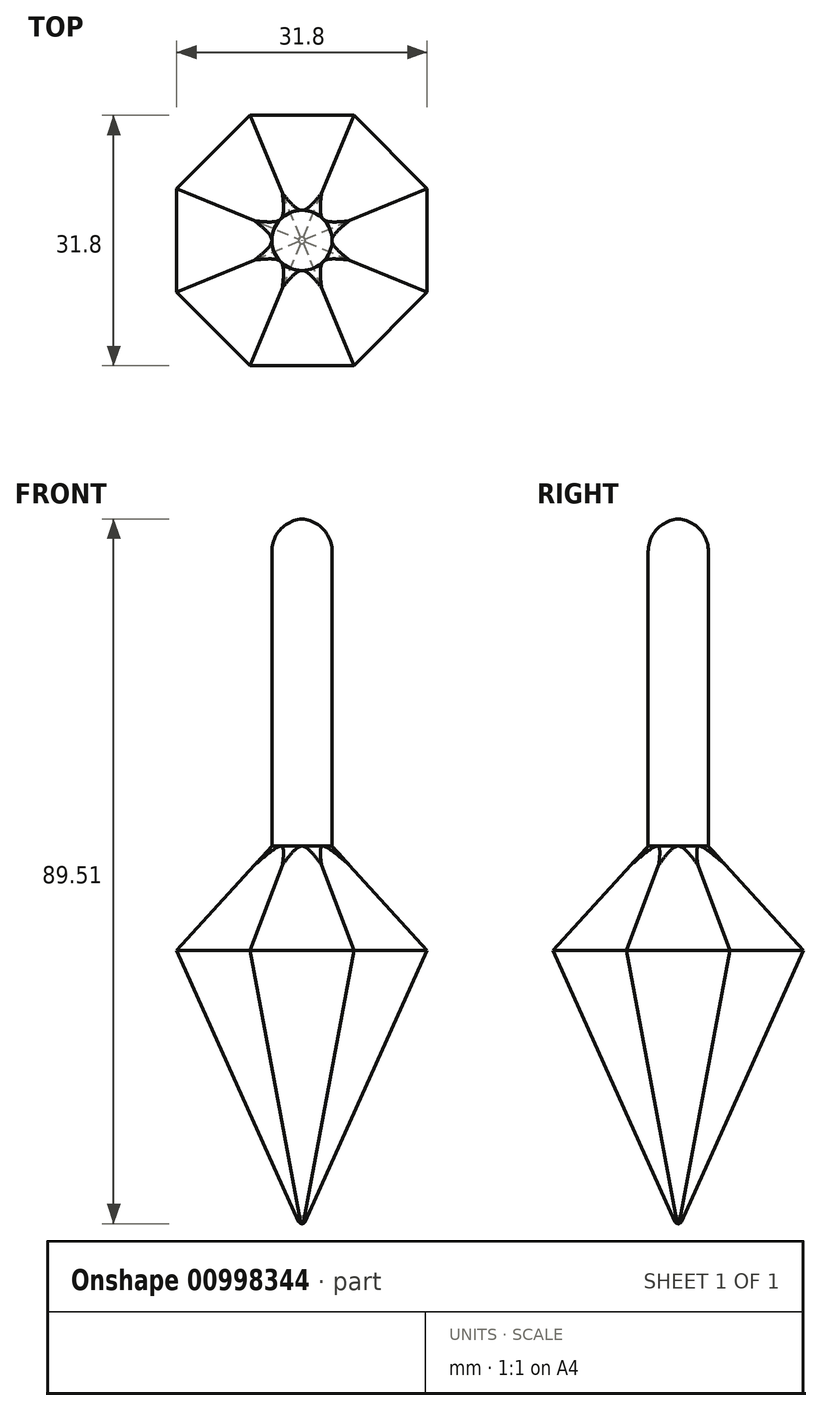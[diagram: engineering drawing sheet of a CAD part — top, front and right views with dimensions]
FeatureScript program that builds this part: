
annotation { "Feature Type Name" : "Feature", "Feature Type Description" : "" }
export const myFeature = defineFeature(function(context is Context, id is Id, definition is map)
    precondition{}
    {
        {
            var Q0;
            Q0=qCreatedBy(makeId("Front.planeOp"),FACE);
            var sketch = newSketch(context, id + "F0", { "sketchPlane" : qUnion([Q0])});
            skLineSegment(sketch, "E0", {"start": v(0, 0) * mm, "end": v(-18.62, 35.4) * mm});
            skLineSegment(sketch, "E1", {"start": v(-18.62, 35.4) * mm, "end": v(-3.83, 48.61) * mm});
            skLineSegment(sketch, "E2", {"start": v(-3.83, 48.61) * mm, "end": v(-3.83, 86.06) * mm});
            skLineSegment(sketch, "E3", {"start": v(0, 86.06) * mm, "end": v(0, 0) * mm});
            skArc(sketch, "E4", {"start": v(0, 90.17) * mm, "mid": v(-2.72, 88.86) * mm, "end": v(-3.83, 86.06) * mm});
            skLineSegment(sketch, "E5", {"start": v(0, 90.17) * mm, "end": v(0, 86.06) * mm});
            skLineSegment(sketch, "E6", {"start": v(0, 0) * mm, "end": v(-41.43, 0) * mm, "construction": true});
            skSolve(sketch);
        }
        {
            var Q0;
            Q0=makeQuery(id+"F0.imprint","IMPRINT",FACE,{"disambiguationData":[TD([[makeQuery(id+"F0.imprint","IMPRINT",EDGE,{"derivedFrom":sQuery(id+"F0.wireOp",EDGE,"E0")}),-1.0]])]});
            var Q1;
            Q1=sQuery(id+"F0.wireOp",EDGE,"E3");
            revolve(context, id + "F1", {"surfaceOperationType" : NewSurfaceOperationType.NEW, "entities" : qUnion([Q0]), "axis" : qUnion([Q1]), "revolveType" : RevolveType.FULL});
        }
        {
            var Q0;
            Q0=qCreatedBy(makeId("Front.planeOp"),FACE);
            var sketch = newSketch(context, id + "F2", { "sketchPlane" : qUnion([Q0])});
            skLineSegment(sketch, "E7", {"start": v(0, 0) * mm, "end": v(-15.9, 35.38) * mm});
            skLineSegment(sketch, "E8", {"start": v(-15.9, 35.38) * mm, "end": v(-23.42, 35.38) * mm});
            skLineSegment(sketch, "E9", {"start": v(-23.42, 35.38) * mm, "end": v(0, 0) * mm});
            skLineSegment(sketch, "E10", {"start": v(-15.9, 35.38) * mm, "end": v(-3.83, 48.61) * mm});
            skLineSegment(sketch, "E11", {"start": v(-3.83, 48.61) * mm, "end": v(-23.42, 35.38) * mm});
            skSolve(sketch);
        }
        {
            var Q0;
            Q0 = qSketchRegion(id + "F2", true);
            extrude(context, id + "F3", {"entities" : qUnion([Q0]), "endBound" : BoundingType.SYMMETRIC, "depth" : 26 * mm, "offsetDistance" : 25 * mm});
        }
        {
            var Q0;
            Q0=makeQuery(id+"F3.opExtrude","SWEPT_BODY",BODY,{"disambiguationData":[OSD([sQuery(id+"F2.wireOp",EDGE,"E7"),sQuery(id+"F2.wireOp",EDGE,"E9"),sQuery(id+"F2.wireOp",EDGE,"E10"),sQuery(id+"F2.wireOp",EDGE,"E11")])]});
            var Q1;
            Q1=makeQuery(id+"F1.opRevolve","SWEPT_EDGE",EDGE,{"disambiguationData":[OSD([sQuery(id+"F0.wireOp",EDGE,"E0"),sQuery(id+"F0.wireOp",EDGE,"E1")])]});
            circularPattern(context, id + "F4", {"entities" : qUnion([Q0]), "axis" : qUnion([Q1]), "angle" : 360 * degree, "instanceCount" : 8, "equalSpace" : true});
        }
        {
            var Q0;
            Q0=makeQuery(id+"F3.opExtrude","SWEPT_BODY",BODY,{"disambiguationData":[OSD([sQuery(id+"F2.wireOp",EDGE,"E7"),sQuery(id+"F2.wireOp",EDGE,"E9"),sQuery(id+"F2.wireOp",EDGE,"E10"),sQuery(id+"F2.wireOp",EDGE,"E11")])]});
            var Q1;
            Q1=makeQuery(id+"F4.opPattern","COPY",BODY,{"derivedFrom":makeQuery(id+"F3.opExtrude","SWEPT_BODY",BODY,{"disambiguationData":[OSD([sQuery(id+"F2.wireOp",EDGE,"E7"),sQuery(id+"F2.wireOp",EDGE,"E9"),sQuery(id+"F2.wireOp",EDGE,"E10"),sQuery(id+"F2.wireOp",EDGE,"E11")])]}),"instanceName":"1"});
            var Q2;
            Q2=makeQuery(id+"F4.opPattern","COPY",BODY,{"derivedFrom":makeQuery(id+"F3.opExtrude","SWEPT_BODY",BODY,{"disambiguationData":[OSD([sQuery(id+"F2.wireOp",EDGE,"E7"),sQuery(id+"F2.wireOp",EDGE,"E9"),sQuery(id+"F2.wireOp",EDGE,"E10"),sQuery(id+"F2.wireOp",EDGE,"E11")])]}),"instanceName":"2"});
            var Q3;
            Q3=makeQuery(id+"F4.opPattern","COPY",BODY,{"derivedFrom":makeQuery(id+"F3.opExtrude","SWEPT_BODY",BODY,{"disambiguationData":[OSD([sQuery(id+"F2.wireOp",EDGE,"E7"),sQuery(id+"F2.wireOp",EDGE,"E9"),sQuery(id+"F2.wireOp",EDGE,"E10"),sQuery(id+"F2.wireOp",EDGE,"E11")])]}),"instanceName":"3"});
            var Q4;
            Q4=makeQuery(id+"F4.opPattern","COPY",BODY,{"derivedFrom":makeQuery(id+"F3.opExtrude","SWEPT_BODY",BODY,{"disambiguationData":[OSD([sQuery(id+"F2.wireOp",EDGE,"E7"),sQuery(id+"F2.wireOp",EDGE,"E9"),sQuery(id+"F2.wireOp",EDGE,"E10"),sQuery(id+"F2.wireOp",EDGE,"E11")])]}),"instanceName":"4"});
            var Q5;
            Q5=makeQuery(id+"F4.opPattern","COPY",BODY,{"derivedFrom":makeQuery(id+"F3.opExtrude","SWEPT_BODY",BODY,{"disambiguationData":[OSD([sQuery(id+"F2.wireOp",EDGE,"E7"),sQuery(id+"F2.wireOp",EDGE,"E9"),sQuery(id+"F2.wireOp",EDGE,"E10"),sQuery(id+"F2.wireOp",EDGE,"E11")])]}),"instanceName":"5"});
            var Q6;
            Q6=makeQuery(id+"F4.opPattern","COPY",BODY,{"derivedFrom":makeQuery(id+"F3.opExtrude","SWEPT_BODY",BODY,{"disambiguationData":[OSD([sQuery(id+"F2.wireOp",EDGE,"E7"),sQuery(id+"F2.wireOp",EDGE,"E9"),sQuery(id+"F2.wireOp",EDGE,"E10"),sQuery(id+"F2.wireOp",EDGE,"E11")])]}),"instanceName":"6"});
            var Q7;
            Q7=makeQuery(id+"F4.opPattern","COPY",BODY,{"derivedFrom":makeQuery(id+"F3.opExtrude","SWEPT_BODY",BODY,{"disambiguationData":[OSD([sQuery(id+"F2.wireOp",EDGE,"E7"),sQuery(id+"F2.wireOp",EDGE,"E9"),sQuery(id+"F2.wireOp",EDGE,"E10"),sQuery(id+"F2.wireOp",EDGE,"E11")])]}),"instanceName":"7"});
            var Q8;
            Q8=makeQuery(id+"F1.opRevolve","SWEPT_BODY",BODY,{"disambiguationData":[OSD([sQuery(id+"F0.wireOp",EDGE,"E0"),sQuery(id+"F0.wireOp",EDGE,"E1"),sQuery(id+"F0.wireOp",EDGE,"E2"),sQuery(id+"F0.wireOp",EDGE,"E3"),sQuery(id+"F0.wireOp",EDGE,"E4"),sQuery(id+"F0.wireOp",EDGE,"E5")])]});
            booleanBodies(context, id + "F5", {"operationType" : BooleanOperationType.SUBTRACTION, "tools" : qUnion([Q0, Q1, Q2, Q3, Q4, Q5, Q6, Q7]), "targets" : qUnion([Q8])});
        }
        {
            var Q0;
            Q0=qCreatedBy(makeId("Front.planeOp"),FACE);
            var sketch = newSketch(context, id + "F6", { "sketchPlane" : qUnion([Q0])});
            skPoint(sketch, "E12", {"position": v(0.42, 0.93) * mm});
            skLineSegment(sketch, "E13", {"start": v(0.42, 0.93) * mm, "end": v(0, 0) * mm});
            skArc(sketch, "E14", {"start": v(0, 0.66) * mm, "mid": v(0.25, 0.73) * mm, "end": v(0.42, 0.93) * mm});
            skLineSegment(sketch, "E15", {"start": v(0, 0.66) * mm, "end": v(0, 0) * mm});
            skLineSegment(sketch, "E16", {"start": v(0.42, 0.93) * mm, "end": v(0.53, 0.84) * mm});
            skLineSegment(sketch, "E17", {"start": v(0.53, 0.84) * mm, "end": v(0.1, -0.23) * mm});
            skLineSegment(sketch, "E18", {"start": v(0.1, -0.23) * mm, "end": v(0, 0) * mm});
            skSolve(sketch);
        }
        {
            var Q0;
            Q0=makeQuery(id+"F6.imprint","IMPRINT",FACE,{"disambiguationData":[TD([[makeQuery(id+"F6.imprint","IMPRINT",EDGE,{"derivedFrom":sQuery(id+"F6.wireOp",EDGE,"E13")}),1.0]])]});
            var Q1;
            Q1=makeQuery(id+"F6.imprint","IMPRINT",FACE,{"disambiguationData":[TD([[makeQuery(id+"F6.imprint","IMPRINT",EDGE,{"derivedFrom":sQuery(id+"F6.wireOp",EDGE,"E13")}),-1.0]])]});
            var Q2;
            Q2=sQuery(id+"F6.wireOp",EDGE,"E15");
            revolve(context, id + "F7", {"operationType" : NewBodyOperationType.REMOVE, "surfaceOperationType" : NewSurfaceOperationType.NEW, "entities" : qUnion([Q0, Q1]), "axis" : qUnion([Q2]), "revolveType" : RevolveType.FULL, "oppositeDirection" : true});
        }
    });
